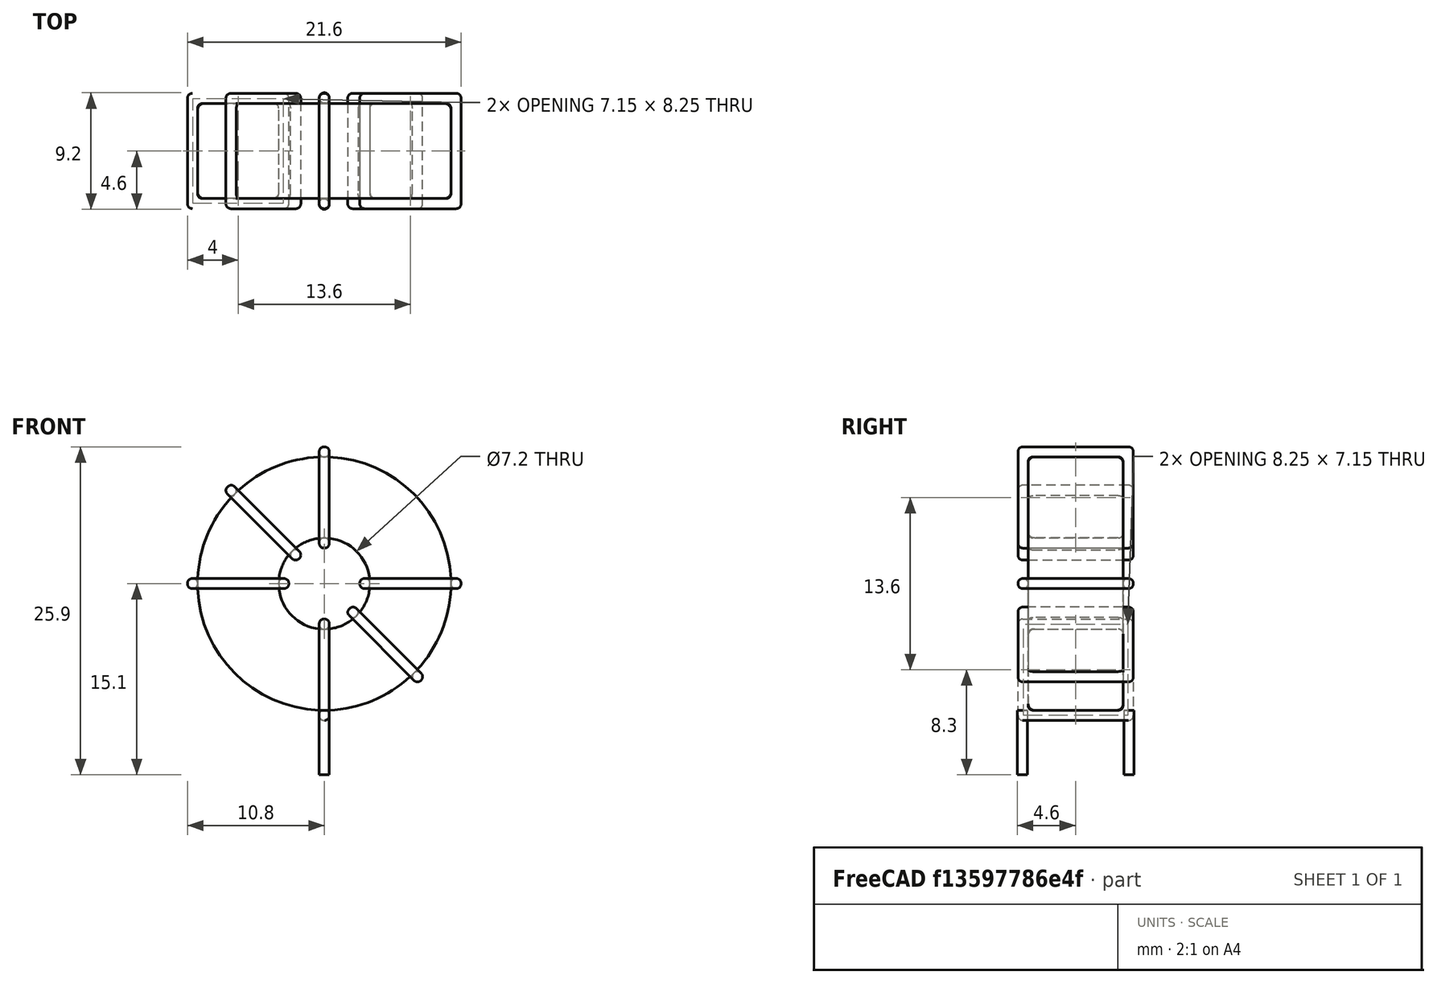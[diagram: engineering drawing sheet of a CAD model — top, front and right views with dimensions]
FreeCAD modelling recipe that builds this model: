
FCSTD DOCUMENT  (FreeCAD 0.16R6703 (Git))
Label: L_Radial_round_toroid_vertical_master
License: All rights reserved
LicenseURL: http://en.wikipedia.org/wiki/All_rights_reserved
objects: Sketcher::SketchObject×6, PartDesign::Pad×6, PartDesign::Fillet×5, Spreadsheet::Sheet×1
note: 23 computed .brp shape members not serialized (recipe doc carries the construction recipe); baked Part::Feature solids carry a one-line shape summary decoded from their .brp

FEATURE [Spreadsheet::Sheet] Spreadsheet  label="dimensions"
  cells = A1=Wx; B1(Wx)=21.6; C1(WW)=7.2; A2=Wy; B2(Wy)=9.1; A3=RM; B3(RMx)=8.4; C3(RMy)=0; A4=d_wire; B4(d_wire)=0.8; A5=H; B5(H)=21.6; A6=offsetx; B6(offsetx)=10.8
FEATURE [Sketcher::SketchObject] Sketch
  Placement = pos=(0,-4.2,0) rot=(1,0,0;1.5708rad)
  expr: Placement.Base.y = -Spreadsheet.RMx / 2
  expr: Constraints[0] = Spreadsheet.Wx / 2 - Spreadsheet.d_wire
  expr: Constraints[4] = Spreadsheet.WW / 2
  expr: Constraints[2] = Spreadsheet.Wx / 2 + Spreadsheet.d_wire + 0.5
  sketch-geometry (2):
    g0: Circle CenterX=0 CenterY=12.1 CenterZ=0 NormalX=0 NormalY=0 NormalZ=1 Radius=10
    g1: Circle CenterX=0 CenterY=12.1 CenterZ=0 NormalX=0 NormalY=0 NormalZ=1 Radius=3.6
  constraints (5):
    c: Radius(g0) = 10
    c: DistanceX(g-1,g0) = 0
    c: DistanceY(g-1,g0) = 12.1
    c: Coincident(g1,g0)
    c: Radius(g1) = 3.6
FEATURE [PartDesign::Pad] Pad
  Length = 7.5
  Length2 = 100
  Midplane = true
  Placement = pos=(0,-4.2,0) rot=(1,0,0;1.5708rad)
  Sketch = -> Sketch
  Type = 0
  expr: Length = Spreadsheet.Wy - 2 * Spreadsheet.d_wire
FEATURE [Sketcher::SketchObject] Sketch001
  Placement = pos=(0,0,1.3) rot=(0,0,1;0rad)
  expr: Placement.Base.z = 0.5 + Spreadsheet.d_wire
  expr: Constraints[4] = Spreadsheet.RMy
  expr: Constraints[2] = -Spreadsheet.RMx
  expr: Constraints[1] = Spreadsheet.d_wire / 2
  sketch-geometry (2):
    g0: Circle CenterX=0 CenterY=0 CenterZ=0 NormalX=0 NormalY=0 NormalZ=1 Radius=0.4
    g1: Circle CenterX=0 CenterY=-8.4 CenterZ=0 NormalX=0 NormalY=0 NormalZ=1 Radius=0.4
  constraints (5):
    c: Equal(g0,g1)
    c: Radius(g0) = 0.4
    c: DistanceY(g-1,g1) = -8.4
    c: Coincident(g0,g-1)
    c: DistanceX(g-1,g1) = 0
FEATURE [PartDesign::Pad] Pad001
  Length = 0.8
  Length2 = 4.3
  Placement = pos=(0,0,1.3) rot=(0,0,1;0rad)
  Reversed = true
  Sketch = -> Sketch001
  Type = 4
  expr: Length2 = 3.5 + Spreadsheet.d_wire
  expr: Length = Spreadsheet.d_wire
FEATURE [PartDesign::Fillet] Fillet
  Base = -> Pad [Edge6,Edge3,Edge2]
  Placement = pos=(0,-4.2,0) rot=(1,0,0;1.5708rad)
  Radius = 0.5
FEATURE [Sketcher::SketchObject] Sketch003
  Placement = pos=(0,0.35,12.1) rot=(1,0,0;3.14159rad)
  expr: Constraints[18] = Spreadsheet.d_wire
  expr: Constraints[16] = Spreadsheet.d_wire
  expr: Constraints[19] = Spreadsheet.d_wire
  expr: Constraints[17] = Spreadsheet.d_wire
  expr: Placement.Base.y = -1 * (Spreadsheet.RMx - Spreadsheet.Wy) / 2
  expr: Constraints[21] = (Spreadsheet.Wx - Spreadsheet.WW) / 2 - Spreadsheet.d_wire
  expr: Constraints[22] = Spreadsheet.Wx / 2 - Spreadsheet.d_wire
  expr: Constraints[43] = Spreadsheet.d_wire
  expr: Constraints[48] = Spreadsheet.Wx - Spreadsheet.d_wire * 2
  expr: Constraints[49] = Spreadsheet.Wy
  expr: Placement.Base.z = Spreadsheet.Wx / 2 + Spreadsheet.d_wire + 0.5
  sketch-geometry (16):
    g0: LineSegment StartX=-2.8 StartY=0 StartZ=0 EndX=-10.8 EndY=0 EndZ=0
    g1: LineSegment StartX=-10.8 StartY=0 StartZ=0 EndX=-10.8 EndY=9.1 EndZ=0
    g2: LineSegment StartX=-10.8 StartY=9.1 StartZ=0 EndX=-2.8 EndY=9.1 EndZ=0
    g3: LineSegment StartX=-2.8 StartY=9.1 StartZ=0 EndX=-2.8 EndY=0 EndZ=0
    g4: LineSegment StartX=-10 StartY=8.3 StartZ=0 EndX=-3.6 EndY=8.3 EndZ=0
    g5: LineSegment StartX=-3.6 StartY=8.3 StartZ=0 EndX=-3.6 EndY=0.8 EndZ=0
    g6: LineSegment StartX=-3.6 StartY=0.8 StartZ=0 EndX=-10 EndY=0.8 EndZ=0
    g7: LineSegment StartX=-10 StartY=0.8 StartZ=0 EndX=-10 EndY=8.3 EndZ=0
    g8: LineSegment StartX=2.8 StartY=9.1 StartZ=0 EndX=10.8 EndY=9.1 EndZ=0
    g9: LineSegment StartX=10.8 StartY=9.1 StartZ=0 EndX=10.8 EndY=0 EndZ=0
    g10: LineSegment StartX=10.8 StartY=0 StartZ=0 EndX=2.8 EndY=0 EndZ=0
    g11: LineSegment StartX=2.8 StartY=0 StartZ=0 EndX=2.8 EndY=9.1 EndZ=0
    g12: LineSegment StartX=3.6 StartY=8.3 StartZ=0 EndX=10 EndY=8.3 EndZ=0
    g13: LineSegment StartX=10 StartY=8.3 StartZ=0 EndX=10 EndY=0.8 EndZ=0
    g14: LineSegment StartX=10 StartY=0.8 StartZ=0 EndX=3.6 EndY=0.8 EndZ=0
    g15: LineSegment StartX=3.6 StartY=0.8 StartZ=0 EndX=3.6 EndY=8.3 EndZ=0
  constraints (50):
    c: Horizontal(g0)
    c: Coincident(g1,g0)
    c: Vertical(g1)
    c: Coincident(g2,g1)
    c: Horizontal(g2)
    c: Coincident(g3,g2)
    c: Coincident(g3,g0)
    c: Vertical(g3)
    c: Coincident(g4,g5)
    c: Coincident(g5,g6)
    c: Coincident(g6,g7)
    c: Coincident(g7,g4)
    c: Horizontal(g4)
    c: Horizontal(g6)
    c: Vertical(g5)
    c: Vertical(g7)
    c: DistanceX(g1,g4) = 0.8
    c: DistanceY(g4,g1) = 0.8
    c: DistanceX(g5,g0) = 0.8
    c: DistanceY(g0,g5) = 0.8
    c: DistanceY(g-1,g0) = 0
    c: DistanceX(g6,g6) = 6.4
    c: DistanceX(g6,g-1) = 10
    c: Coincident(g8,g9)
    c: Coincident(g9,g10)
    c: Coincident(g10,g11)
    c: Coincident(g11,g8)
    c: Horizontal(g8)
    c: Horizontal(g10)
    c: Vertical(g9)
    c: Vertical(g11)
    c: Coincident(g12,g13)
    c: Coincident(g13,g14)
    c: Coincident(g14,g15)
    c: Coincident(g15,g12)
    c: Horizontal(g12)
    c: Horizontal(g14)
    c: Vertical(g13)
    c: Vertical(g15)
    c: DistanceY(g8,g2) = 0
    c: DistanceY(g10,g0) = 0
    c: DistanceY(g14,g5) = 0
    c: DistanceY(g12,g4) = 0
    c: DistanceX(g8,g12) = 0.8
    c: Equal(g8,g2)
    c: Equal(g12,g4)
    c: Equal(g9,g1)
    c: Equal(g13,g7)
    c: DistanceX(g4,g12) = 20
    c: DistanceY(g0,g1) = 9.1
FEATURE [PartDesign::Pad] Pad002
  Length = 0.8
  Length2 = 100
  Midplane = true
  Placement = pos=(0,0.35,12.1) rot=(1,0,0;3.14159rad)
  Sketch = -> Sketch003
  Type = 0
  expr: Length = Spreadsheet.d_wire
FEATURE [PartDesign::Fillet] Fillet001
  Base = -> Pad002 [Edge38,Edge41,Edge42,Edge43,Edge29,Edge32,Edge33,Edge34,Edge25,Edge35,Edge36,Edge13,Edge14,Edge15,Edge16,Edge17,Edge18,Edge19,Edge1,Edge2,Edge3,Edge4,Edge5,Edge6,Edge7,Edge37,Edge39,Edge40,Edge20,Edge23,Edge24,Edge21,Edge22,Edge8,Edge9,Edge10,Edge11,Edge12,Edge26,Edge27,+8 more]
  Placement = pos=(0,0.35,12.1) rot=(1,0,0;3.14159rad)
  Radius = 0.376
  expr: Radius = Spreadsheet.d_wire * 0.47
FEATURE [Sketcher::SketchObject] Sketch004
  Placement = pos=(0,0.35,12.1) rot=(0.92388,0,0.382683;3.14159rad)
  expr: Constraints[18] = Spreadsheet.d_wire
  expr: Constraints[16] = Spreadsheet.d_wire
  expr: Constraints[19] = Spreadsheet.d_wire
  expr: Constraints[17] = Spreadsheet.d_wire
  expr: Placement.Base.y = -1 * (Spreadsheet.RMx - Spreadsheet.Wy) / 2
  expr: Constraints[21] = (Spreadsheet.Wx - Spreadsheet.WW) / 2 - Spreadsheet.d_wire
  expr: Constraints[22] = Spreadsheet.Wx / 2 - Spreadsheet.d_wire
  expr: Constraints[43] = Spreadsheet.d_wire
  expr: Constraints[48] = Spreadsheet.Wx - 2 * Spreadsheet.d_wire
  expr: Constraints[49] = Spreadsheet.Wy
  expr: Placement.Base.z = Spreadsheet.Wx / 2 + Spreadsheet.d_wire + 0.5
  sketch-geometry (16):
    g0: LineSegment StartX=-2.8 StartY=0 StartZ=0 EndX=-10.8 EndY=0 EndZ=0
    g1: LineSegment StartX=-10.8 StartY=0 StartZ=0 EndX=-10.8 EndY=9.1 EndZ=0
    g2: LineSegment StartX=-10.8 StartY=9.1 StartZ=0 EndX=-2.8 EndY=9.1 EndZ=0
    g3: LineSegment StartX=-2.8 StartY=9.1 StartZ=0 EndX=-2.8 EndY=0 EndZ=0
    g4: LineSegment StartX=-10 StartY=8.3 StartZ=0 EndX=-3.6 EndY=8.3 EndZ=0
    g5: LineSegment StartX=-3.6 StartY=8.3 StartZ=0 EndX=-3.6 EndY=0.8 EndZ=0
    g6: LineSegment StartX=-3.6 StartY=0.8 StartZ=0 EndX=-10 EndY=0.8 EndZ=0
    g7: LineSegment StartX=-10 StartY=0.8 StartZ=0 EndX=-10 EndY=8.3 EndZ=0
    g8: LineSegment StartX=2.8 StartY=9.1 StartZ=0 EndX=10.8 EndY=9.1 EndZ=0
    g9: LineSegment StartX=10.8 StartY=9.1 StartZ=0 EndX=10.8 EndY=0 EndZ=0
    g10: LineSegment StartX=10.8 StartY=0 StartZ=0 EndX=2.8 EndY=0 EndZ=0
    g11: LineSegment StartX=2.8 StartY=0 StartZ=0 EndX=2.8 EndY=9.1 EndZ=0
    g12: LineSegment StartX=3.6 StartY=8.3 StartZ=0 EndX=10 EndY=8.3 EndZ=0
    g13: LineSegment StartX=10 StartY=8.3 StartZ=0 EndX=10 EndY=0.8 EndZ=0
    g14: LineSegment StartX=10 StartY=0.8 StartZ=0 EndX=3.6 EndY=0.8 EndZ=0
    g15: LineSegment StartX=3.6 StartY=0.8 StartZ=0 EndX=3.6 EndY=8.3 EndZ=0
  constraints (50):
    c: Horizontal(g0)
    c: Coincident(g1,g0)
    c: Vertical(g1)
    c: Coincident(g2,g1)
    c: Horizontal(g2)
    c: Coincident(g3,g2)
    c: Coincident(g3,g0)
    c: Vertical(g3)
    c: Coincident(g4,g5)
    c: Coincident(g5,g6)
    c: Coincident(g6,g7)
    c: Coincident(g7,g4)
    c: Horizontal(g4)
    c: Horizontal(g6)
    c: Vertical(g5)
    c: Vertical(g7)
    c: DistanceX(g1,g4) = 0.8
    c: DistanceY(g4,g1) = 0.8
    c: DistanceX(g5,g0) = 0.8
    c: DistanceY(g0,g5) = 0.8
    c: DistanceY(g-1,g0) = 0
    c: DistanceX(g6,g6) = 6.4
    c: DistanceX(g6,g-1) = 10
    c: Coincident(g8,g9)
    c: Coincident(g9,g10)
    c: Coincident(g10,g11)
    c: Coincident(g11,g8)
    c: Horizontal(g8)
    c: Horizontal(g10)
    c: Vertical(g9)
    c: Vertical(g11)
    c: Coincident(g12,g13)
    c: Coincident(g13,g14)
    c: Coincident(g14,g15)
    c: Coincident(g15,g12)
    c: Horizontal(g12)
    c: Horizontal(g14)
    c: Vertical(g13)
    c: Vertical(g15)
    c: DistanceY(g8,g2) = 0
    c: DistanceY(g10,g0) = 0
    c: DistanceY(g14,g5) = 0
    c: DistanceY(g12,g4) = 0
    c: DistanceX(g8,g12) = 0.8
    c: Equal(g8,g2)
    c: Equal(g12,g4)
    c: Equal(g9,g1)
    c: Equal(g13,g7)
    c: DistanceX(g4,g12) = 20
    c: DistanceY(g0,g1) = 9.1
FEATURE [PartDesign::Pad] Pad003
  Length = 0.8
  Length2 = 100
  Midplane = true
  Placement = pos=(0,0.35,12.1) rot=(0.92388,0,0.382683;3.14159rad)
  Sketch = -> Sketch004
  Type = 0
  expr: Length = Spreadsheet.d_wire
FEATURE [PartDesign::Fillet] Fillet002
  Base = -> Pad003 [Edge38,Edge41,Edge42,Edge43,Edge29,Edge32,Edge33,Edge34,Edge25,Edge35,Edge36,Edge13,Edge14,Edge15,Edge16,Edge17,Edge18,Edge19,Edge1,Edge2,Edge3,Edge4,Edge5,Edge6,Edge7,Edge37,Edge39,Edge40,Edge20,Edge23,Edge24,Edge21,Edge22,Edge8,Edge9,Edge10,Edge11,Edge12,Edge26,Edge27,+8 more]
  Placement = pos=(0,0.35,12.1) rot=(0.92388,0,0.382683;3.14159rad)
  Radius = 0.376
  expr: Radius = Spreadsheet.d_wire * 0.47
FEATURE [Sketcher::SketchObject] Sketch005
  Placement = pos=(0,0.35,12.1) rot=(0.92388,0,-0.382683;3.14159rad)
  expr: Constraints[18] = Spreadsheet.d_wire
  expr: Constraints[16] = Spreadsheet.d_wire
  expr: Constraints[19] = Spreadsheet.d_wire
  expr: Constraints[17] = Spreadsheet.d_wire
  expr: Placement.Base.y = -1 * (Spreadsheet.RMx - Spreadsheet.Wy) / 2
  expr: Constraints[21] = (Spreadsheet.Wx - Spreadsheet.WW) / 2 - Spreadsheet.d_wire
  expr: Constraints[22] = Spreadsheet.Wx / 2 - Spreadsheet.d_wire
  expr: Constraints[43] = Spreadsheet.d_wire
  expr: Constraints[48] = Spreadsheet.Wx - 2 * Spreadsheet.d_wire
  expr: Constraints[49] = Spreadsheet.Wy
  expr: Placement.Base.z = Spreadsheet.Wx / 2 + Spreadsheet.d_wire + 0.5
  sketch-geometry (16):
    g0: LineSegment StartX=-2.8 StartY=0 StartZ=0 EndX=-10.8 EndY=0 EndZ=0
    g1: LineSegment StartX=-10.8 StartY=0 StartZ=0 EndX=-10.8 EndY=9.1 EndZ=0
    g2: LineSegment StartX=-10.8 StartY=9.1 StartZ=0 EndX=-2.8 EndY=9.1 EndZ=0
    g3: LineSegment StartX=-2.8 StartY=9.1 StartZ=0 EndX=-2.8 EndY=0 EndZ=0
    g4: LineSegment StartX=-10 StartY=8.3 StartZ=0 EndX=-3.6 EndY=8.3 EndZ=0
    g5: LineSegment StartX=-3.6 StartY=8.3 StartZ=0 EndX=-3.6 EndY=0.8 EndZ=0
    g6: LineSegment StartX=-3.6 StartY=0.8 StartZ=0 EndX=-10 EndY=0.8 EndZ=0
    g7: LineSegment StartX=-10 StartY=0.8 StartZ=0 EndX=-10 EndY=8.3 EndZ=0
    g8: LineSegment StartX=2.8 StartY=9.1 StartZ=0 EndX=10.8 EndY=9.1 EndZ=0
    g9: LineSegment StartX=10.8 StartY=9.1 StartZ=0 EndX=10.8 EndY=0 EndZ=0
    g10: LineSegment StartX=10.8 StartY=0 StartZ=0 EndX=2.8 EndY=0 EndZ=0
    g11: LineSegment StartX=2.8 StartY=0 StartZ=0 EndX=2.8 EndY=9.1 EndZ=0
    g12: LineSegment StartX=3.6 StartY=8.3 StartZ=0 EndX=10 EndY=8.3 EndZ=0
    g13: LineSegment StartX=10 StartY=8.3 StartZ=0 EndX=10 EndY=0.8 EndZ=0
    g14: LineSegment StartX=10 StartY=0.8 StartZ=0 EndX=3.6 EndY=0.8 EndZ=0
    g15: LineSegment StartX=3.6 StartY=0.8 StartZ=0 EndX=3.6 EndY=8.3 EndZ=0
  constraints (50):
    c: Horizontal(g0)
    c: Coincident(g1,g0)
    c: Vertical(g1)
    c: Coincident(g2,g1)
    c: Horizontal(g2)
    c: Coincident(g3,g2)
    c: Coincident(g3,g0)
    c: Vertical(g3)
    c: Coincident(g4,g5)
    c: Coincident(g5,g6)
    c: Coincident(g6,g7)
    c: Coincident(g7,g4)
    c: Horizontal(g4)
    c: Horizontal(g6)
    c: Vertical(g5)
    c: Vertical(g7)
    c: DistanceX(g1,g4) = 0.8
    c: DistanceY(g4,g1) = 0.8
    c: DistanceX(g5,g0) = 0.8
    c: DistanceY(g0,g5) = 0.8
    c: DistanceY(g-1,g0) = 0
    c: DistanceX(g6,g6) = 6.4
    c: DistanceX(g6,g-1) = 10
    c: Coincident(g8,g9)
    c: Coincident(g9,g10)
    c: Coincident(g10,g11)
    c: Coincident(g11,g8)
    c: Horizontal(g8)
    c: Horizontal(g10)
    c: Vertical(g9)
    c: Vertical(g11)
    c: Coincident(g12,g13)
    c: Coincident(g13,g14)
    c: Coincident(g14,g15)
    c: Coincident(g15,g12)
    c: Horizontal(g12)
    c: Horizontal(g14)
    c: Vertical(g13)
    c: Vertical(g15)
    c: DistanceY(g8,g2) = 0
    c: DistanceY(g10,g0) = 0
    c: DistanceY(g14,g5) = 0
    c: DistanceY(g12,g4) = 0
    c: DistanceX(g8,g12) = 0.8
    c: Equal(g8,g2)
    c: Equal(g12,g4)
    c: Equal(g9,g1)
    c: Equal(g13,g7)
    c: DistanceX(g4,g12) = 20
    c: DistanceY(g0,g1) = 9.1
FEATURE [PartDesign::Pad] Pad004
  Length = 0.8
  Length2 = 100
  Midplane = true
  Placement = pos=(0,0.35,12.1) rot=(0.92388,0,-0.382683;3.14159rad)
  Sketch = -> Sketch005
  Type = 0
  expr: Length = Spreadsheet.d_wire
FEATURE [PartDesign::Fillet] Fillet003
  Base = -> Pad004 [Edge38,Edge41,Edge42,Edge43,Edge29,Edge32,Edge33,Edge34,Edge25,Edge35,Edge36,Edge13,Edge14,Edge15,Edge16,Edge17,Edge18,Edge19,Edge1,Edge2,Edge3,Edge4,Edge5,Edge6,Edge7,Edge37,Edge39,Edge40,Edge20,Edge23,Edge24,Edge21,Edge22,Edge8,Edge9,Edge10,Edge11,Edge12,Edge26,Edge27,+8 more]
  Placement = pos=(0,0.35,12.1) rot=(0.92388,0,-0.382683;3.14159rad)
  Radius = 0.376
  expr: Radius = Spreadsheet.d_wire * 0.47
FEATURE [Sketcher::SketchObject] Sketch006
  Placement = pos=(0,0.35,12.1) rot=(0.707107,0,0.707107;3.14159rad)
  expr: Constraints[18] = Spreadsheet.d_wire
  expr: Constraints[16] = Spreadsheet.d_wire
  expr: Constraints[19] = Spreadsheet.d_wire
  expr: Constraints[17] = Spreadsheet.d_wire
  expr: Placement.Base.y = -1 * (Spreadsheet.RMx - Spreadsheet.Wy) / 2
  expr: Constraints[21] = (Spreadsheet.Wx - Spreadsheet.WW) / 2 - Spreadsheet.d_wire
  expr: Constraints[22] = Spreadsheet.Wx / 2 - Spreadsheet.d_wire
  expr: Constraints[43] = Spreadsheet.d_wire
  expr: Constraints[48] = Spreadsheet.Wx - Spreadsheet.d_wire * 2
  expr: Constraints[49] = Spreadsheet.Wy
  expr: Placement.Base.z = Spreadsheet.Wx / 2 + Spreadsheet.d_wire + 0.5
  sketch-geometry (16):
    g0: LineSegment StartX=-2.8 StartY=0 StartZ=0 EndX=-10.8 EndY=0 EndZ=0
    g1: LineSegment StartX=-10.8 StartY=0 StartZ=0 EndX=-10.8 EndY=9.1 EndZ=0
    g2: LineSegment StartX=-10.8 StartY=9.1 StartZ=0 EndX=-2.8 EndY=9.1 EndZ=0
    g3: LineSegment StartX=-2.8 StartY=9.1 StartZ=0 EndX=-2.8 EndY=0 EndZ=0
    g4: LineSegment StartX=-10 StartY=8.3 StartZ=0 EndX=-3.6 EndY=8.3 EndZ=0
    g5: LineSegment StartX=-3.6 StartY=8.3 StartZ=0 EndX=-3.6 EndY=0.8 EndZ=0
    g6: LineSegment StartX=-3.6 StartY=0.8 StartZ=0 EndX=-10 EndY=0.8 EndZ=0
    g7: LineSegment StartX=-10 StartY=0.8 StartZ=0 EndX=-10 EndY=8.3 EndZ=0
    g8: LineSegment StartX=2.8 StartY=9.1 StartZ=0 EndX=10.8 EndY=9.1 EndZ=0
    g9: LineSegment StartX=10.8 StartY=9.1 StartZ=0 EndX=10.8 EndY=0 EndZ=0
    g10: LineSegment StartX=10.8 StartY=0 StartZ=0 EndX=2.8 EndY=0 EndZ=0
    g11: LineSegment StartX=2.8 StartY=0 StartZ=0 EndX=2.8 EndY=9.1 EndZ=0
    g12: LineSegment StartX=3.6 StartY=8.3 StartZ=0 EndX=10 EndY=8.3 EndZ=0
    g13: LineSegment StartX=10 StartY=8.3 StartZ=0 EndX=10 EndY=0.8 EndZ=0
    g14: LineSegment StartX=10 StartY=0.8 StartZ=0 EndX=3.6 EndY=0.8 EndZ=0
    g15: LineSegment StartX=3.6 StartY=0.8 StartZ=0 EndX=3.6 EndY=8.3 EndZ=0
  constraints (50):
    c: Horizontal(g0)
    c: Coincident(g1,g0)
    c: Vertical(g1)
    c: Coincident(g2,g1)
    c: Horizontal(g2)
    c: Coincident(g3,g2)
    c: Coincident(g3,g0)
    c: Vertical(g3)
    c: Coincident(g4,g5)
    c: Coincident(g5,g6)
    c: Coincident(g6,g7)
    c: Coincident(g7,g4)
    c: Horizontal(g4)
    c: Horizontal(g6)
    c: Vertical(g5)
    c: Vertical(g7)
    c: DistanceX(g1,g4) = 0.8
    c: DistanceY(g4,g1) = 0.8
    c: DistanceX(g5,g0) = 0.8
    c: DistanceY(g0,g5) = 0.8
    c: DistanceY(g-1,g0) = 0
    c: DistanceX(g6,g6) = 6.4
    c: DistanceX(g6,g-1) = 10
    c: Coincident(g8,g9)
    c: Coincident(g9,g10)
    c: Coincident(g10,g11)
    c: Coincident(g11,g8)
    c: Horizontal(g8)
    c: Horizontal(g10)
    c: Vertical(g9)
    c: Vertical(g11)
    c: Coincident(g12,g13)
    c: Coincident(g13,g14)
    c: Coincident(g14,g15)
    c: Coincident(g15,g12)
    c: Horizontal(g12)
    c: Horizontal(g14)
    c: Vertical(g13)
    c: Vertical(g15)
    c: DistanceY(g8,g2) = 0
    c: DistanceY(g10,g0) = 0
    c: DistanceY(g14,g5) = 0
    c: DistanceY(g12,g4) = 0
    c: DistanceX(g8,g12) = 0.8
    c: Equal(g8,g2)
    c: Equal(g12,g4)
    c: Equal(g9,g1)
    c: Equal(g13,g7)
    c: DistanceX(g4,g12) = 20
    c: DistanceY(g0,g1) = 9.1
FEATURE [PartDesign::Pad] Pad005
  Length = 0.8
  Length2 = 100
  Midplane = true
  Placement = pos=(0,0.35,12.1) rot=(0.707107,0,0.707107;3.14159rad)
  Sketch = -> Sketch006
  Type = 0
  expr: Length = Spreadsheet.d_wire
FEATURE [PartDesign::Fillet] Fillet004
  Base = -> Pad005 [Edge38,Edge41,Edge42,Edge43,Edge29,Edge32,Edge33,Edge34,Edge25,Edge35,Edge36,Edge13,Edge14,Edge15,Edge16,Edge17,Edge18,Edge19,Edge1,Edge2,Edge3,Edge4,Edge5,Edge6,Edge7,Edge37,Edge39,Edge40,Edge20,Edge23,Edge24,Edge21,Edge22,Edge8,Edge9,Edge10,Edge11,Edge12,Edge26,Edge27,+8 more]
  Placement = pos=(0,0.35,12.1) rot=(0.707107,0,0.707107;3.14159rad)
  Radius = 0.376
  expr: Radius = Spreadsheet.d_wire * 0.47
